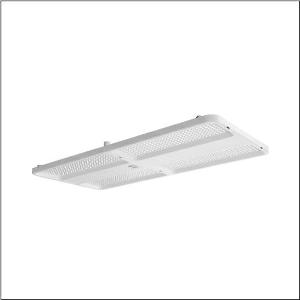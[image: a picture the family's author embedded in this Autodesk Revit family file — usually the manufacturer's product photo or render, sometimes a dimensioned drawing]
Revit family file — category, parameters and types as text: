
# Revit family: highbay_21_maxi_52hn11db4qda03
name_source: partatom
category: Lighting Fixtures
units: mm (PartAtom-declared; Revit-internal decimal feet)

## family parameters
Cut with Voids When Loaded = No
Host = Face
Light Source = No
Part Type = Normal
Room Calculation Point = No
Round Connector Dimension = Use Diameter
Shared = No

## types (1)
- --- (1 x LED, 38000 lm, 197.7 W, 4000K)
    Apparent Load = 198 VA
    CIE Flux Codes = 89 97 99 100 100
    Color Rendering = 80
    Color Temperature = 4000K
    Default Elevation = 1800 mm
    Description = high bay luminaire Highbay 21 maxi; direct symmetric narrow distribution, light control with lens of PMMA; UGR ≤ 19 (X = 4H | Y = 8H | S = 0.25H | reflection values 70/50/20); luminous flux: 38.000lm; light colour: 840, colour temperature: 4000K, MacAdam ≤ 3 SDCM (initial), colour rendering: CRI > 80; luminous efficacy: 192,2lm/W; rated service life: 75.000h (L80) at AT= ta max; control: DALI 2; for wired networking: open and standardized DALI2 interface enables full flexibility and future-proofing for changes in use or functional adaptation through individual programming; multi-sensor luminaire consisting of a DALI2 multi-sensor and DALI2 ECG; multi-sensor luminaire for wired connection to a DALI2 application controller (e.g., SITECO Connect 11 or 21); can also be connected to existing on-site lighting or building automation systems upon request; integrated DALI2 sensor certified according to IEC 62386, Parts 101, 103, 303, and 304; integrated DALI2 ECG provides luminaire data (according to IEC 62386, Part 251), energy data (Part 252), and monitoring and analytics data (Part 253) to higher-level systems for further processing; luminaire with PIR sensor (passive-infrared); with light sensor; luminaire connection: terminal, 5-pole, max. 2.5mm² (cable entry for one cable, Ø 8.5..16mm); mains connection: 230..240V, AC 50/60Hz; connected load: 197,7W; protection rating (complete): IP65; insulation class (complete): insulation class I (protective earthing); protection symbol: D; certification: CE, UKCA; internal wiring halogen-free; luminaire LABS conformity tested according to VDMA 24364:2018-05; Suitable for use in the food industry according to the specifications of IFS-Food, HACCP and/or BRC; housing frame of high-performance plastic PA6, matt traffic white (RAL 9016); cover of PMMA; dimension (LxWxH): 946 x 442 x 72mm; permissible operating ambient temperature: -20..+40°C (reducing of maximum allowable ambient temperature of 5°C with ceiling mounting); packaging unit: 1 piece; (delivery without accessories; please order mounting accessories separately)
    Height = 72 mm  [stored 0.23622 ft]
    Lamp = 1 x LED
    Lamp Light Flux = 38000 lm
    Lamp Power = 197.7 W
    Lamp count = 1
    Length = 946 mm
    Luminous efficacy = 192 lm/W
    Manufacturer = Siteco
    ModVariant = No
    Model = 52HN11DB4QDA03
    Mounting Place = Ceiling
    Mounting Type = Pendant
    Number of Poles = 1
    OnlyDefault = Yes
    Power Factor = 1
    Product Name = Highbay 21 maxi
    Product group = high bay luminaire
    ProductGroupID = 902
    Protection Class = Protection class I
    Protection Degree = IP 65
    RLX_Detail_Level = 1
    RLX_Emergency_Light_Flux = 0 lm
    RLX_Emergency_Type = 0
    RLX_Emergency_Type_DB = No
    RlxData = <blob elided: 128101 chars, md5=229eac81>
    Socket = socket
    Standby Power = 0 W
    System Light Flux = 38000 lm
    System Power = 198 W
    Type Comments = factory setting: luminous flux: 100 % | dim-lin: 254 | 918 mA
    Type Image = l_1363267.jpg
    URL = http://relux.com
    VarID = @adj_012239
    Voltage = 0 V
    Weight = 0.00 kg
    Width = 442 mm

note: [stored X ft] marks values corroborated as IEEE doubles in the binary element streams (Revit-internal decimal feet)

## geometry (parser evidence)
native form markers: Blend x4, Sweep x10
no freeform markers — native parametric forms only
